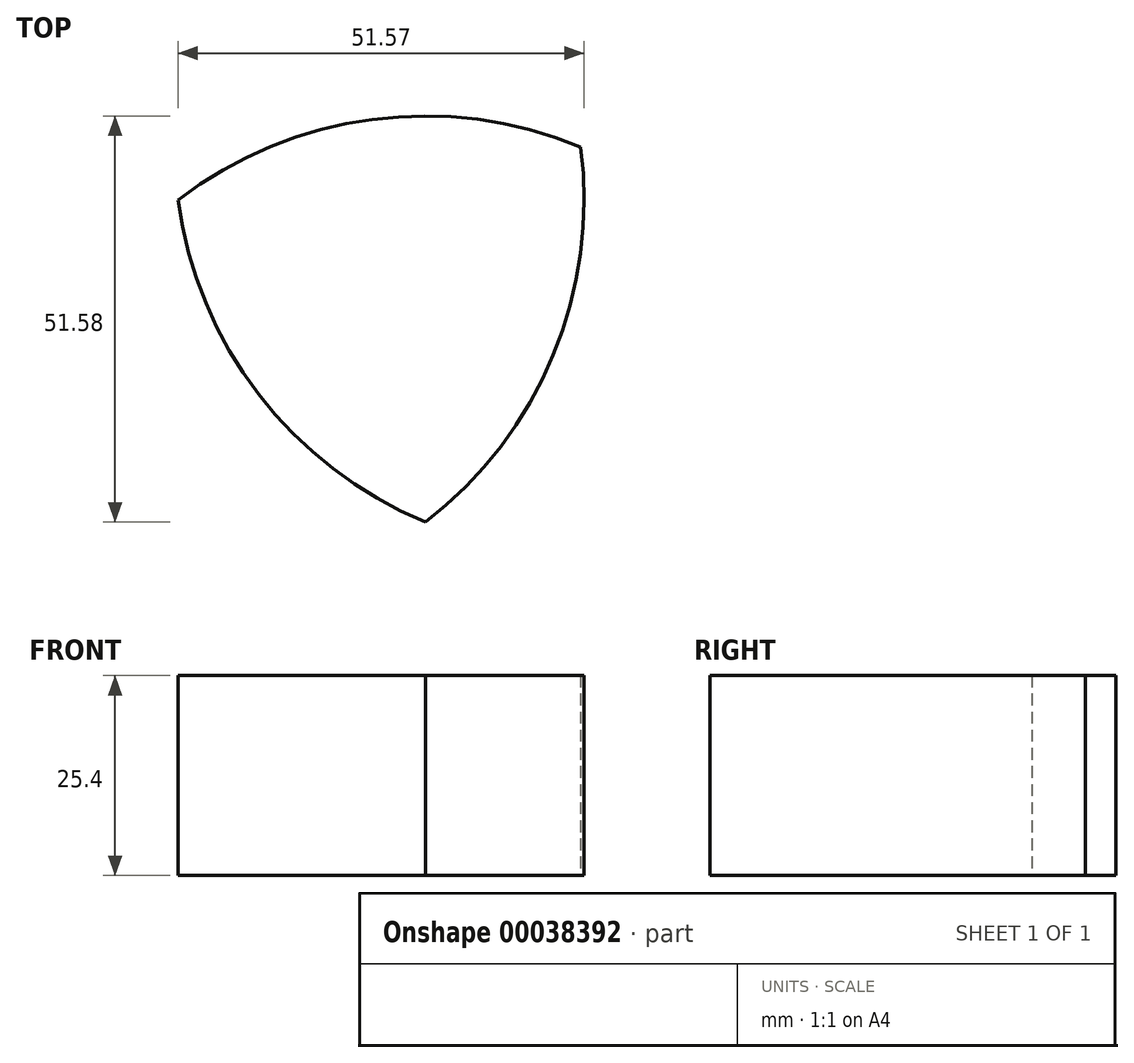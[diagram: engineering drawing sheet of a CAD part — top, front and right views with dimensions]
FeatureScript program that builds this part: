
annotation { "Feature Type Name" : "Feature", "Feature Type Description" : "" }
export const myFeature = defineFeature(function(context is Context, id is Id, definition is map)
    precondition{}
    {
        {
            var Q0;
            Q0=qCreatedBy(makeId("Top.planeOp"),FACE);
            var sketch = newSketch(context, id + "F0", { "sketchPlane" : qUnion([Q0])});
            skCircle(sketch, "E0", {"center": v(0, 0) * mm, "radius": 51.58 * mm});
            skCircle(sketch, "E1", {"center": v(-51.13, -6.75) * mm, "radius": 51.58 * mm});
            skCircle(sketch, "E2", {"center": v(-19.73, -47.66) * mm, "radius": 51.58 * mm});
            skSolve(sketch);
        }
        {
            var Q0;
            {var subQ0=sQuery(id+"F0.wireOp",EDGE,"E2");var subQ3=sQuery(id+"F0.wireOp",EDGE,"E0");var subQ4=makeQuery(id+"F0.imprint","INTERSECT",VERTEX,{"disambiguationData":[OD(1.0)],"derivedFrom":[subQ3,subQ0]});Q0=makeQuery(id+"F0.imprint","IMPRINT",FACE,{"disambiguationData":[TD([[makeQuery(id+"F0.imprint","IMPRINT",EDGE,{"disambiguationData":[TD([[subQ4,-1.0]])],"derivedFrom":subQ3}),1.0]])]});}
            extrude(context, id + "F1", {"entities" : qUnion([Q0]), "depth" : 25.4 * mm});
        }
    });
